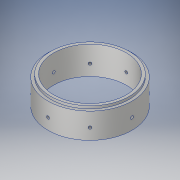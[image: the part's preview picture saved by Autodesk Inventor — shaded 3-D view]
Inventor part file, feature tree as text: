
AUTODESK INVENTOR PART (.ipt)
format: ipt  version: 2017 SP1 (Build 210196100, 196)  size: 192,000 bytes
history: native  units: in
note: dims shown in document units (in); Inventor stores cm internally (conversion verified against a paired STEP export)
features: sketch x2, revolve x1, plane x1, hole x1, pattern_circular x1
ambient origin geometry x8: Origin, YZ Plane, XZ Plane, XY Plane, X Axis, Y Axis, Z Axis, Center Point
bodies: Solid1 (feature_tree)
feature tree (6):
  revolve  "Revolution1"  [1 undecoded]
  plane  "Work Plane1"
  hole  "Hole1"  [1 undecoded]
  pattern_circular  "Circular Pattern1"  [2 undecoded]
  sketch  "Sketch1"  dims[d0=1.13in d1=3.75in]
  sketch  "Sketch2"  dims[d2=0.125in d3=0.1718in d5=1.0in d6=1.0in d7=90.0deg d8=0.5in d9=15.0deg d12=1.25in d13=0.25in d16=0.5in d17=0.5in d18=0.5in d19=2.5in d20=0.5in d22=0.375in d23=0.25in d25=0.234in d27=0.125in d28=0.25in d29=1.0in d30=4.25in d31=0.25in d33=0.8014in d34=15.0deg d35=0.125in d36=1.0in d37=90.0deg d38=0.25in d39=0.75in d40=0.375in d41=0.25in d42=0.5635in d43=1.0in d44=0.8108in d45=3.1496in d46=360.0deg d48=1.0in]
note: 4 required parameter values undecoded (feature->parameter linkage not recoverable at this tier; creation-order binding heuristic only, values carry confidence <= 0.55)